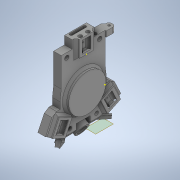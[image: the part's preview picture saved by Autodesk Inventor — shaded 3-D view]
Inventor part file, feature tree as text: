
AUTODESK INVENTOR PART (.ipt)
format: ipt  version: 2022 (Build 260153000, 153)  size: 697,344 bytes
history: native  units: mm
features: sketch x26, extrude x23, other x10, chamfer x9, reference x9, fillet x5, mirror x3, plane x3, projected_geometry x3, revolve x1
ambient origin geometry x8: Origin, YZ Plane, XZ Plane, XY Plane, X Axis, Y Axis, Z Axis, Center Point
bodies: Solid1 (feature_tree)
feature tree (92):
  extrude  "Extrusion1"  Depth=39.9mm
  extrude  "Extrusion3"  Depth=4.0mm
  extrude  "Extrusion4"  Depth=4.95mm
  extrude  "Extrusion5"  Depth=15.0mm
  extrude  "Extrusion6"  Depth=20.0mm
  mirror  "Mirror1"
  chamfer  "Chamfer1"  Distance=3.0mm
  extrude  "Extrusion7"  Depth=3.175mm TaperAngle=0.0deg
  extrude  "Extrusion8"  TaperAngle=0.0deg  [1 undecoded]
  mirror  "Mirror2"
  chamfer  "Chamfer3"  Distance=2.2mm
  extrude  "Extrusion9"  Depth=4.0mm
  plane  "Work Plane1"
  extrude  "Extrusion10"  Depth=3.5mm
  chamfer  "Chamfer4"  Distance=3.0mm
  plane  "Work Plane2"
  extrude  "Extrusion12"  Depth=4.0mm
  fillet  "Fillet3"  Radius=14.0mm
  extrude  "Extrusion15"  Depth=3.5mm
  chamfer  "Chamfer5"  Distance=3.5mm
  chamfer  "Chamfer6"  Distance=2.2mm
  fillet  "Fillet5"  Radius=2.2mm
  extrude  "Extrusion17"  Depth=4.0mm
  chamfer  "Chamfer7"  Distance=3.0mm
  extrude  "Extrusion18"  Depth=4.0mm TaperAngle=0.0deg
  mirror  "Mirror3"
  fillet  "Fillet7"  Radius=1.0mm
  fillet  "Fillet8"  Radius=73.064607mm
  fillet  "Fillet9"  Radius=45.0mm
  extrude  "Extrusion19"  Depth=3.5mm
  chamfer  "Chamfer8"  Distance=3.5mm
  extrude  "Extrusion20"  Depth=4.0mm
  revolve  "Revolution1"  [1 undecoded]
  extrude  "Extrusion21"  Depth=4.0mm
  extrude  "Extrusion22"  Depth=4.0mm
  chamfer  "Chamfer9"  Distance=7.75mm
  extrude  "Extrusion23"  Depth=4.0mm
  extrude  "Extrusion24"  Depth=4.0mm
  chamfer  "Chamfer10"  Distance=3.0mm
  extrude  "Extrusion25"  TaperAngle=0.0deg  [1 undecoded]
  plane  "Work Plane3"
  extrude  "Extrusion26"  TaperAngle=0.0deg  [1 undecoded]
  sketch  "Sketch31"  dims[d62=9.0mm]
  sketch  "Sketch32"  dims[d63=8.0mm]
  extrude  "Extrusion27"  Depth=4.0mm TaperAngle=0.0deg
  extrude  "Extrusion28"  Depth=4.0mm TaperAngle=45.0deg
  sketch  "Sketch1"  dims[d0=15.0mm d1=39.9mm]
  sketch  "Sketch3"  dims[d2=7.0mm d3=0.0mm d8=4.0mm]
  sketch  "Sketch4"  dims[d9=4.25mm d10=4.95mm]
  sketch  "Sketch6"  dims[d11=50.0mm d12=15.0mm]
  sketch  "Sketch7"  dims[d14=7.5mm d15=20.0mm]
  sketch  "Sketch8"  dims[d17=3.75mm]
  sketch  "Sketch9"  dims[d18=20.0mm d38=3.0mm d39=0.0mm]
  reference  "Reference1"
  reference  "Reference2"
  reference  "Reference3"
  reference  "Reference4"
  reference  "Reference5"
  reference  "Reference6"
  sketch  "Sketch11"  dims[d40=25.9mm d41=3.175mm d42=0.0mm]
  projected_geometry  "Projected Loop4"
  sketch  "Sketch13"  dims[d46=180.0deg d47=0.0mm]
  sketch  "Sketch15"  dims[d48=15.0mm]
  sketch  "Sketch18"  dims[d49=13.0mm]
  projected_geometry  "Projected Loop6"
  sketch  "Sketch20"  dims[d50=0.0mm]
  sketch  "Sketch21"  dims[d51=0.0mm]
  sketch  "Sketch22"  dims[d52=15.0mm]
  sketch  "Sketch23"  dims[d53=13.0mm]
  sketch  "Sketch24"  dims[d54=0.0mm]
  reference  "Reference11"
  sketch  "Sketch25"  dims[d55=20.0mm]
  sketch  "Sketch26"  dims[d56=3.5mm]
  sketch  "Sketch27"  dims[d57=10.0mm]
  reference  "Reference12"
  sketch  "Sketch28"  dims[d58=5.0mm]
  reference  "Reference13"
  sketch  "Sketch29"  dims[d60=5.0mm]
  projected_geometry  "Projected Loop7"
  sketch  "Sketch30"  dims[d61=8.0mm]
  sketch  "Sketch33"  dims[d64=9.0mm]
  sketch  "Sketch34"  dims[d65=3.5mm d66=2.2mm d67=3.0mm d68=3.5mm d69=3.0mm d70=2.2mm d71=14.0mm d72=0.0mm d73=3.5mm d74=3.5mm d75=2.2mm d76=2.2mm d77=3.0mm d78=3.0mm d79=14.0mm d80=0.0mm d81=1.0mm d82=2.0mm d83=45.0deg d89=73.064607mm d90=45.0mm d91=3.5mm d92=3.5mm d93=4.0mm d94=4.0mm d95=4.0mm d96=4.0mm d97=7.75mm d98=0.0mm d99=1.0mm d100=1.0mm d101=3.0mm d102=0.0mm d103=0.0mm d104=7.75mm d105=0.0mm d106=3.0mm d107=2.0mm d108=45.0deg d109=15.0mm d110=4.0mm d111=3.175mm d112=0.0mm d113=-3.175mm d114=0.6mm d115=0.0mm d116=2.0mm d117=2.0mm d118=45.0deg d121=-3.5mm d124=15.0mm d125=20.0mm d126=2.5mm d127=0.0mm d128=0.0mm d129=2.5mm d130=0.0mm d131=1.25mm d140=5.0mm d141=0.0mm d142=10.0mm d143=10.0mm d144=4.0mm d145=5.0mm d146=45.0deg d147=4.0mm d148=5.0mm d149=45.0deg d150=1.5mm d161=0.4mm d162=30.0mm d163=7.0mm d164=10.0mm d165=5.0mm d166=0.0mm d167=3.0mm d168=5.0mm d169=45.0deg d170=21.0mm d171=0.0mm d172=0.3mm d173=1.3mm d174=1.0mm d175=1.0mm d176=20.0mm d177=2.0mm d178=0.0mm d179=1.2mm d180=5.0mm d181=45.0deg d182=5.0mm d183=4.0mm d184=0.0mm d185=0.0mm d186=0.0mm d187=4.0mm d188=30.0deg d189=5.0mm d190=5.0mm d191=25.0mm d192=5.0mm d193=2.0mm d194=2.5mm d195=1.0mm d196=90.0deg d198=4.0mm d199=0.0mm d202=20.0mm d203=4.0mm d204=4.0mm d205=0.0mm d206=4.0mm d207=1.5mm d208=5.0mm d209=45.0deg d210=2.0mm d211=0.2mm d212=5.0mm d213=0.0mm d214=0.2mm d215=5.0mm d216=0.0mm d217=2.0mm d218=5.0mm d219=45.0deg d220=2.0mm d221=0.0mm d222=5.0mm d223=6.5mm d224=0.0mm d225=1.0mm d226=11.0mm d227=8.0mm d228=5.5mm d229=8.0mm d230=11.0mm d231=1.0mm d232=5.5mm d233=4.0mm d234=6.5mm d235=0.0mm d236=25.9mm d237=6.5mm d238=0.0mm]
  parser-record x2  (decoder bookkeeping rows leaked as tree rows — omitted from the tree; the rows remain in map.json)
  other  "speedyPrinty.iam"
  other  "V-Slot 20x40x500 Linear Rail:11"
  other  "Y gantry printed v33_1:3"
  other  "gantry top (1):1"
  other  "Tool holder.iam"
  other  "Volcano_Printhead:1"
  other  "E3D-VOLCANO-1.75-MO:2"
  other  "D2HW_C202M:5"
note: 4 required parameter values undecoded (feature->parameter linkage not recoverable at this tier; creation-order binding heuristic only, values carry confidence <= 0.55)
note: 2 file-system paths scrubbed to <path> (originals preserved in map.json)